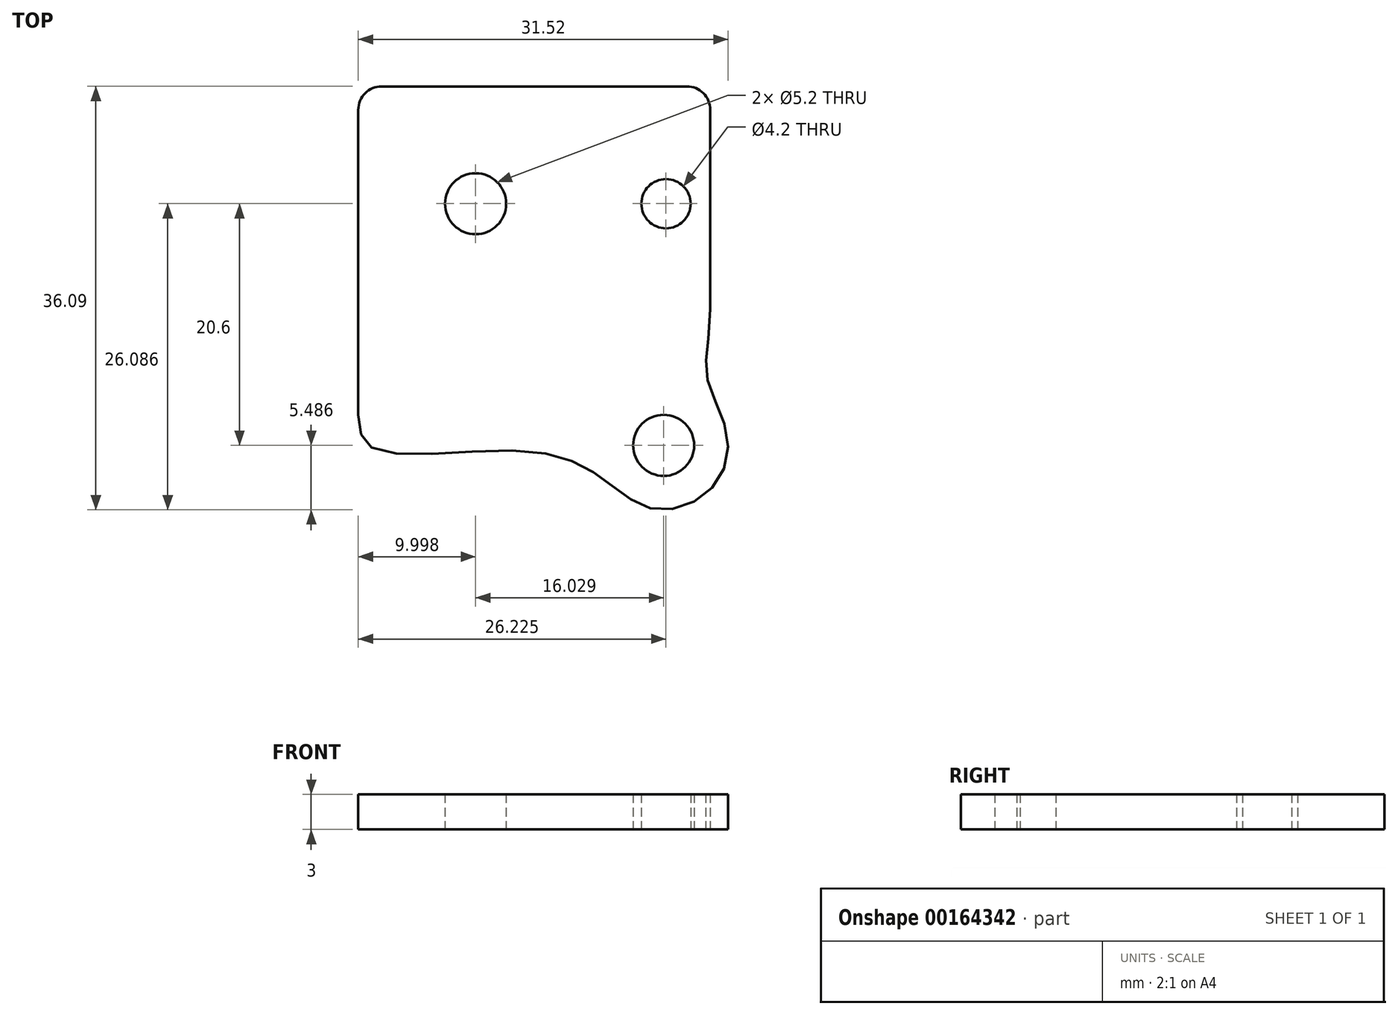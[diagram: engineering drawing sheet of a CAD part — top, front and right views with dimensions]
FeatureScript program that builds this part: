
annotation { "Feature Type Name" : "Feature", "Feature Type Description" : "" }
export const myFeature = defineFeature(function(context is Context, id is Id, definition is map)
    precondition{}
    {
        {
            var Q0;
            Q0=qCreatedBy(makeId("Top.planeOp"),FACE);
            var sketch = newSketch(context, id + "F0", { "sketchPlane" : qUnion([Q0])});
            skLineSegment(sketch, "E0.bottom", {"start": v(-13.65, 7.9) * mm, "end": v(12.35, 7.9) * mm});
            skLineSegment(sketch, "E0.left", {"start": v(-15.65, 5.9) * mm, "end": v(-15.65, -20.1) * mm});
            skLineSegment(sketch, "E0.right", {"start": v(14.35, 5.9) * mm, "end": v(14.35, -11.17) * mm});
            skCircle(sketch, "E1", {"center": v(10.57, -2.1) * mm, "radius": 2.1 * mm});
            skCircle(sketch, "E2", {"center": v(-5.65, -2.1) * mm, "radius": 2.6 * mm});
            skCircle(sketch, "E3", {"center": v(10.38, -22.7) * mm, "radius": 2.6 * mm});
            skPoint(sketch, "E4.orphan", {"position": v(14.35, -22.1) * mm});
            skPoint(sketch, "E5.visualSharp", {"position": v(-15.65, 7.9) * mm});
            skArc(sketch, "E5.filletArc", {"start": v(-13.65, 7.9) * mm, "mid": v(-15.07, 7.32) * mm, "end": v(-15.65, 5.9) * mm});
            skPoint(sketch, "E6.visualSharp", {"position": v(14.35, 7.9) * mm});
            skArc(sketch, "E6.filletArc", {"start": v(14.35, 5.9) * mm, "mid": v(13.76, 7.32) * mm, "end": v(12.35, 7.9) * mm});
            skPoint(sketch, "E7.visualSharp", {"position": v(14.35, -11.09) * mm});
            skPoint(sketch, "E8.visualSharp", {"position": v(-15.65, -22.1) * mm});
            skPoint(sketch, "E9.visualSharp", {"position": v(6.78, -30.02) * mm});
            skFitSpline(sketch, "E10", {"points": [v(-15.65, -20.1) * mm, v(-14.35, -22.97) * mm, v(-1.46, -23.18) * mm, v(5.2, -25.54) * mm, v(9.52, -28.1) * mm, v(14.22, -26.6) * mm, v(15.82, -22.08) * mm, v(14.06, -16.86) * mm, v(14.35, -11.09) * mm], "startDerivative": vector(2.52, -42.95) * mm, "endDerivative": vector(0.45, 68.55) * mm});
            skLineSegment(sketch, "E11", {"start": v(-5.65, -2.1) * mm, "end": v(36.16, -2.1) * mm, "construction": true});
            skLineSegment(sketch, "E12", {"start": v(36.16, -2.1) * mm, "end": v(36.16, -12.1) * mm, "construction": true});
            skLineSegment(sketch, "E13", {"start": v(36.16, -12.1) * mm, "end": v(-5.65, -12.1) * mm, "construction": true});
            skLineSegment(sketch, "E14", {"start": v(-5.65, -12.1) * mm, "end": v(-5.65, -2.1) * mm, "construction": true});
            skCircle(sketch, "E15", {"center": v(10.38, -22.7) * mm, "radius": 5.48 * mm, "construction": true});
            skSolve(sketch);
        }
        {
            var Q0;
            Q0 = qSketchRegion(id + "F0", true);
            extrude(context, id + "F1", {"entities" : qUnion([Q0]), "depth" : 3 * mm});
        }
    });
